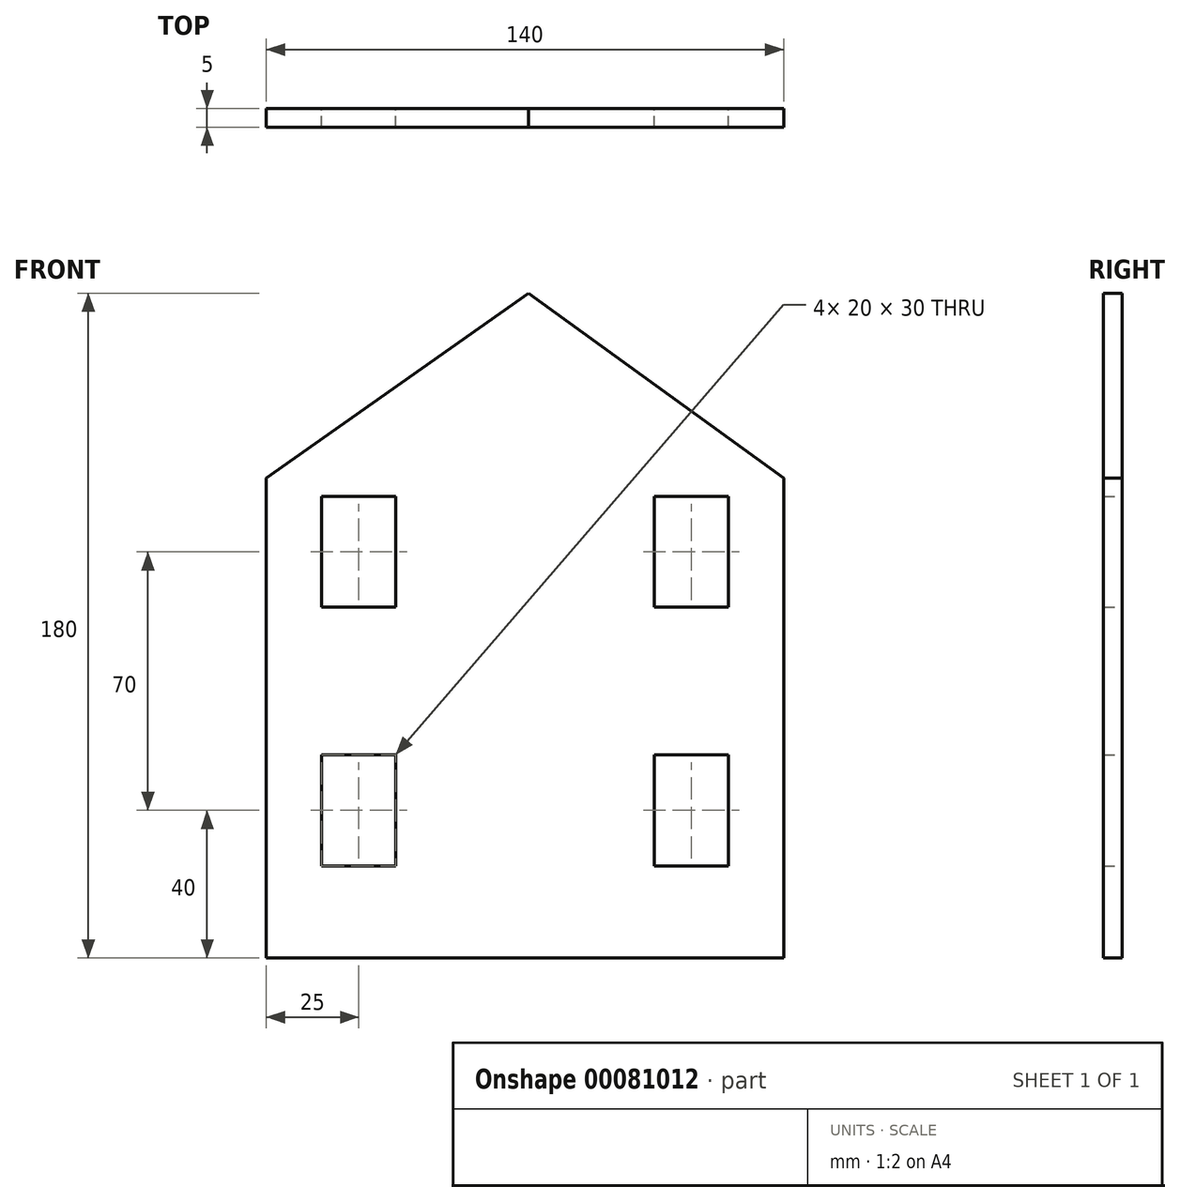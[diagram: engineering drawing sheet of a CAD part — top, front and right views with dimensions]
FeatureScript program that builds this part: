
annotation { "Feature Type Name" : "Feature", "Feature Type Description" : "" }
export const myFeature = defineFeature(function(context is Context, id is Id, definition is map)
    precondition{}
    {
        {
            var Q0;
            Q0=qCreatedBy(makeId("Front.planeOp"),FACE);
            var sketch = newSketch(context, id + "F0", { "sketchPlane" : qUnion([Q0])});
            skLineSegment(sketch, "E0.bottom", {"start": v(0, 0) * mm, "end": v(-140, 0) * mm});
            skLineSegment(sketch, "E0.left", {"start": v(0, 0) * mm, "end": v(0, 130) * mm});
            skLineSegment(sketch, "E1", {"start": v(-69.06, 180) * mm, "end": v(0, 130) * mm});
            skLineSegment(sketch, "E2.bottom", {"start": v(-125, 55) * mm, "end": v(-105, 55) * mm});
            skLineSegment(sketch, "E2.top", {"start": v(-125, 25) * mm, "end": v(-105, 25) * mm});
            skLineSegment(sketch, "E2.left", {"start": v(-125, 55) * mm, "end": v(-125, 25) * mm});
            skLineSegment(sketch, "E2.right", {"start": v(-105, 55) * mm, "end": v(-105, 25) * mm});
            skLineSegment(sketch, "E3", {"start": v(-140, 80) * mm, "end": v(0, 80) * mm});
            skLineSegment(sketch, "E4", {"start": v(-125, 95) * mm, "end": v(-125, 125) * mm});
            skLineSegment(sketch, "E5", {"start": v(-125, 125) * mm, "end": v(-105, 125) * mm});
            skLineSegment(sketch, "E6", {"start": v(-70, 130) * mm, "end": v(-70, 0) * mm, "construction": true});
            skLineSegment(sketch, "E7", {"start": v(-125, 95) * mm, "end": v(-105, 95) * mm});
            skLineSegment(sketch, "E8", {"start": v(-105, 125) * mm, "end": v(-105, 95) * mm});
            skLineSegment(sketch, "E9.MirrorCS", {"start": v(-35, 125) * mm, "end": v(-35, 95) * mm});
            skLineSegment(sketch, "E10.MirrorCS", {"start": v(-15, 95) * mm, "end": v(-35, 95) * mm});
            skLineSegment(sketch, "E11.MirrorCS", {"start": v(-15, 95) * mm, "end": v(-15, 125) * mm});
            skLineSegment(sketch, "E12.MirrorCS", {"start": v(-15, 125) * mm, "end": v(-35, 125) * mm});
            skLineSegment(sketch, "E13.MirrorCS", {"start": v(-35, 55) * mm, "end": v(-35, 25) * mm});
            skLineSegment(sketch, "E14.MirrorCS", {"start": v(-15, 55) * mm, "end": v(-35, 55) * mm});
            skLineSegment(sketch, "E15.MirrorCS", {"start": v(-15, 55) * mm, "end": v(-15, 25) * mm});
            skLineSegment(sketch, "E16.MirrorCS", {"start": v(-15, 25) * mm, "end": v(-35, 25) * mm});
            skLineSegment(sketch, "E17", {"start": v(-140, 0) * mm, "end": v(-140, 80) * mm});
            skLineSegment(sketch, "E18", {"start": v(-140, 80) * mm, "end": v(-140, 130) * mm});
            skLineSegment(sketch, "E19", {"start": v(-140, 130) * mm, "end": v(-69.06, 180) * mm});
            skLineSegment(sketch, "E20", {"start": v(-140, 130) * mm, "end": v(0, 130) * mm, "construction": true});
            skPoint(sketch, "E21", {"position": v(-70, 0) * mm});
            skPoint(sketch, "E22", {"position": v(-70, 130) * mm});
            skSolve(sketch);
        }
        {
            var Q0;
            Q0 = qSketchRegion(id + "F0", true);
            extrude(context, id + "F1", {"entities" : qUnion([Q0]), "endBound" : BoundingType.SYMMETRIC, "depth" : 5 * mm});
        }
    });
